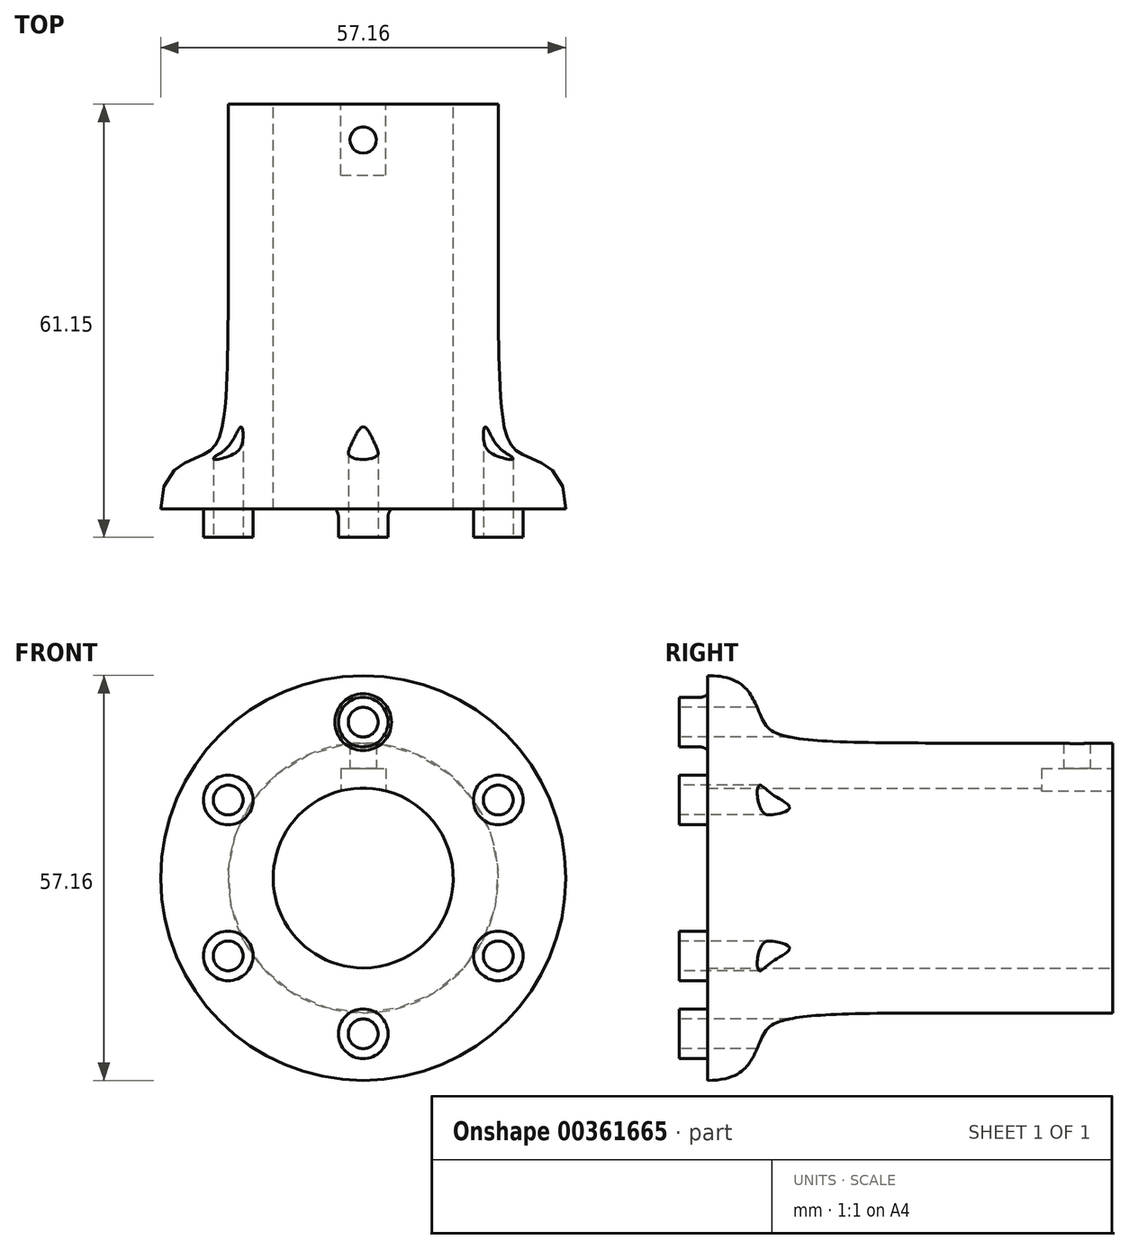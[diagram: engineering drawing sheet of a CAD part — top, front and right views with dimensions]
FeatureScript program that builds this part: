
annotation { "Feature Type Name" : "Feature", "Feature Type Description" : "" }
export const myFeature = defineFeature(function(context is Context, id is Id, definition is map)
    precondition{}
    {
        {
            var Q0;
            Q0=qCreatedBy(makeId("Front.planeOp"),FACE);
            var sketch = newSketch(context, id + "F0", { "sketchPlane" : qUnion([Q0])});
            skCircle(sketch, "E0", {"center": v(0, 0) * mm, "radius": 12.7 * mm});
            skCircle(sketch, "E1", {"center": v(0, 0) * mm, "radius": 19.05 * mm});
            skSolve(sketch);
        }
        {
            var Q0;
            Q0=qSketchRegion(id+"F0",true);
            extrude(context, id + "F1", {"entities" : qUnion([Q0]), "depth" : 25.4 * mm});
        }
        {
            var Q0;
            Q0=qCreatedBy(makeId("Front.planeOp"),FACE);
            cPlane(context, id + "F2", {"entities" : qUnion([Q0]), "cplaneType" : CPlaneType.OFFSET, "offset" : 50.8 * mm, "width" : 152.4 * mm, "height" : 152.4 * mm});
        }
        {
            var Q0;
            Q0=qCreatedBy(id+"F2.planeOp",FACE);
            var sketch = newSketch(context, id + "F3", { "sketchPlane" : qUnion([Q0])});
            skCircle(sketch, "E2", {"center": v(0, 0) * mm, "radius": 25.4 * mm});
            skCircle(sketch, "E3", {"center": v(0, 0) * mm, "radius": 6.35 * mm});
            skSolve(sketch);
        }
        {
            var Q0;
            Q0=qCreatedBy(makeId("Top.planeOp"),FACE);
            var sketch = newSketch(context, id + "F4", { "sketchPlane" : qUnion([Q0])});
            skLineSegment(sketch, "E4", {"start": v(0, 54.57) * mm, "end": v(0, 8.8) * mm, "construction": true});
            skSolve(sketch);
        }
        {
            var Q0;
            Q0=makeQuery(id+"F1.opExtrude","CAP_FACE",FACE,{"disambiguationData":[OSD([sQuery(id+"F0.wireOp",EDGE,"E0"),sQuery(id+"F0.wireOp",EDGE,"E1")])],"isStart":true});
            var sketch = newSketch(context, id + "F5", { "sketchPlane" : qUnion([Q0])});
            skLineSegment(sketch, "E5.bottom", {"start": v(3.18, 15.47) * mm, "end": v(-3.17, 15.47) * mm});
            skLineSegment(sketch, "E5.top", {"start": v(3.18, 9.12) * mm, "end": v(-3.17, 9.12) * mm});
            skLineSegment(sketch, "E5.left", {"start": v(3.18, 15.47) * mm, "end": v(3.18, 9.12) * mm});
            skLineSegment(sketch, "E5.right", {"start": v(-3.17, 15.47) * mm, "end": v(-3.17, 9.12) * mm});
            skPoint(sketch, "E5.middle", {"position": v(0, 12.3) * mm});
            skPoint(sketch, "E6", {"position": v(3.18, 12.3) * mm});
            skPoint(sketch, "E7", {"position": v(-3.17, 12.3) * mm});
            skSolve(sketch);
        }
        {
            var Q0;
            Q0=qSketchRegion(id+"F5",true);
            extrude(context, id + "F6", {"entities" : qUnion([Q0]), "operationType" : NewBodyOperationType.REMOVE, "oppositeDirection" : true, "depth" : 10 * mm, "offsetDistance" : 25.4 * mm});
        }
        {
            var Q0;
            Q0=qCreatedBy(makeId("Top.planeOp"),FACE);
            var sketch = newSketch(context, id + "F7", { "sketchPlane" : qUnion([Q0])});
            skCircle(sketch, "E8", {"center": v(0, -5.04) * mm, "radius": 1.87 * mm});
            skSolve(sketch);
        }
        {
            var Q0;
            Q0=makeQuery(id+"F1.opExtrude","CAP_FACE",FACE,{"disambiguationData":[OSD([sQuery(id+"F0.wireOp",EDGE,"E0"),sQuery(id+"F0.wireOp",EDGE,"E1")])],"isStart":false});
            var sketch = newSketch(context, id + "F8", { "sketchPlane" : qUnion([Q0])});
            skCircle(sketch, "E9.0", {"center": v(0, 0) * mm, "radius": 19.05 * mm});
            skSolve(sketch);
        }
        {
            var Q0;
            Q0=qSketchRegion(id+"F7",true);
            extrude(context, id + "F9", {"entities" : qUnion([Q0]), "operationType" : NewBodyOperationType.REMOVE, "depth" : 25.4 * mm, "offsetDistance" : 25.4 * mm});
        }
        {
            var Q0;
            Q0=qCreatedBy(id+"F2.planeOp",FACE);
            var sketch = newSketch(context, id + "F10", { "sketchPlane" : qUnion([Q0])});
            skCircle(sketch, "E10", {"center": v(0, 0) * mm, "radius": 25.4 * mm});
            skSolve(sketch);
        }
        {
            var Q0;
            Q0=qCreatedBy(id+"F2.planeOp",FACE);
            cPlane(context, id + "F11", {"entities" : qUnion([Q0]), "cplaneType" : CPlaneType.OFFSET, "offset" : 6.35 * mm, "width" : 152.4 * mm, "height" : 152.4 * mm});
        }
        {
            var Q0;
            Q0=qCreatedBy(id+"F11.planeOp",FACE);
            var sketch = newSketch(context, id + "F12", { "sketchPlane" : qUnion([Q0])});
            skCircle(sketch, "E11", {"center": v(0, 0) * mm, "radius": 28.58 * mm});
            skSolve(sketch);
        }
        {
            var Q1;
            Q1 = qSketchRegion(id + "F8", true);
            var Q2;
            Q2 = qSketchRegion(id + "F10", true);
            var Q3;
            Q3 = qSketchRegion(id + "F12", true);
            loft(context, id + "F13", {"operationType" : NewBodyOperationType.ADD, "startCondition" : LoftEndDerivativeType.NORMAL_TO_PROFILE, "startMagnitude" : 3, "endCondition" : LoftEndDerivativeType.NORMAL_TO_PROFILE, "endMagnitude" : 2, "sheetProfilesArray" : [{ "sheetProfileEntities" : qUnion([Q1]) }, { "sheetProfileEntities" : qUnion([Q2]) }, { "sheetProfileEntities" : qUnion([Q3]) }]});
        }
        {
            var Q0;
            Q0=makeQuery(id+"F1.opExtrude","CAP_FACE",FACE,{"disambiguationData":[OSD([sQuery(id+"F0.wireOp",EDGE,"E0"),sQuery(id+"F0.wireOp",EDGE,"E1")])],"isStart":true});
            var sketch = newSketch(context, id + "F14", { "sketchPlane" : qUnion([Q0])});
            skCircle(sketch, "E12", {"center": v(0, 0) * mm, "radius": 12.7 * mm});
            skSolve(sketch);
        }
        {
            var Q0;
            Q0 = qSketchRegion(id + "F14", true);
            extrude(context, id + "F15", {"entities" : qUnion([Q0]), "operationType" : NewBodyOperationType.REMOVE, "endBound" : BoundingType.THROUGH_ALL, "oppositeDirection" : true, "depth" : 25.4 * mm, "offsetDistance" : 25.4 * mm});
        }
        {
            var Q0;
            Q0=makeQuery(id+"F13.opLoft","CAP_FACE",FACE,{"disambiguationData":[OSD([makeQuery(id+"F12.imprint","IMPRINT",FACE,{"disambiguationData":[TD([[makeQuery(id+"F12.imprint","IMPRINT",EDGE,{"derivedFrom":sQuery(id+"F12.wireOp",EDGE,"E11")}),1.0]])]})])],"isStart":true});
            var sketch = newSketch(context, id + "F16", { "sketchPlane" : qUnion([Q0])});
            skCircle(sketch, "E13", {"center": v(0, 22) * mm, "radius": 3.5 * mm});
            skCircle(sketch, "E14.1.0", {"center": v(-19.05, 11) * mm, "radius": 3.5 * mm});
            skCircle(sketch, "E14.2.0", {"center": v(-19.05, -11) * mm, "radius": 3.5 * mm});
            skCircle(sketch, "E14.3.0", {"center": v(0, -22) * mm, "radius": 3.5 * mm});
            skCircle(sketch, "E14.4.0", {"center": v(19.05, -11) * mm, "radius": 3.5 * mm});
            skCircle(sketch, "E14.5.0", {"center": v(19.05, 11) * mm, "radius": 3.5 * mm});
            skPoint(sketch, "E14.center", {"position": v(0, 0) * mm});
            skSolve(sketch);
        }
        {
            var Q0;
            Q0 = qSketchRegion(id + "F16", true);
            extrude(context, id + "F17", {"entities" : qUnion([Q0]), "operationType" : NewBodyOperationType.ADD, "depth" : 4 * mm, "offsetDistance" : 25 * mm});
        }
        {
            var Q0;
            Q0=makeQuery(id+"F17.opExtrude","CAP_FACE",FACE,{"disambiguationData":[OSD([sQuery(id+"F16.wireOp",EDGE,"E13")])],"isStart":false});
            var sketch = newSketch(context, id + "F18", { "sketchPlane" : qUnion([Q0])});
            skCircle(sketch, "E15", {"center": v(0, 22) * mm, "radius": 2.1 * mm});
            skCircle(sketch, "E16.1.0", {"center": v(-19.05, 11) * mm, "radius": 2.1 * mm});
            skCircle(sketch, "E16.2.0", {"center": v(-19.05, -11) * mm, "radius": 2.1 * mm});
            skCircle(sketch, "E16.3.0", {"center": v(0, -22) * mm, "radius": 2.1 * mm});
            skCircle(sketch, "E16.4.0", {"center": v(19.05, -11) * mm, "radius": 2.1 * mm});
            skCircle(sketch, "E16.5.0", {"center": v(19.05, 11) * mm, "radius": 2.1 * mm});
            skPoint(sketch, "E16.center", {"position": v(0, 0) * mm});
            skSolve(sketch);
        }
        {
            var Q0;
            Q0=makeQuery(id+"F17.opExtrude","CAP_FACE",FACE,{"disambiguationData":[OSD([sQuery(id+"F16.wireOp",EDGE,"E13")])],"isStart":false});
            cPlane(context, id + "F19", {"entities" : qUnion([Q0]), "cplaneType" : CPlaneType.OFFSET, "offset" : 3 * mm, "oppositeDirection" : true, "width" : 150 * mm, "height" : 150 * mm});
        }
        {
            var Q0;
            Q0=qCreatedBy(id+"F19.planeOp",FACE);
            var sketch = newSketch(context, id + "F20", { "sketchPlane" : qUnion([Q0])});
            skCircle(sketch, "E17.0", {"center": v(0, 22) * mm, "radius": 3.5 * mm});
            skSolve(sketch);
        }
        {
            var Q0;
            Q0=makeQuery(id+"F13.opLoft","CAP_FACE",FACE,{"disambiguationData":[OSD([makeQuery(id+"F12.imprint","IMPRINT",FACE,{"disambiguationData":[TD([[makeQuery(id+"F12.imprint","IMPRINT",EDGE,{"derivedFrom":sQuery(id+"F12.wireOp",EDGE,"E11")}),1.0]])]})])],"isStart":true});
            var sketch = newSketch(context, id + "F21", { "sketchPlane" : qUnion([Q0])});
            skCircle(sketch, "E18", {"center": v(0, 22) * mm, "radius": 4 * mm});
            skSolve(sketch);
        }
        {
            var Q1;
            Q1 = qSketchRegion(id + "F20", true);
            var Q2;
            Q2 = qSketchRegion(id + "F21", true);
            loft(context, id + "F22", {"operationType" : NewBodyOperationType.ADD, "startCondition" : LoftEndDerivativeType.NORMAL_TO_PROFILE, "startMagnitude" : 1, "endCondition" : LoftEndDerivativeType.TANGENT_TO_PROFILE, "endMagnitude" : 1, "sheetProfilesArray" : [{ "sheetProfileEntities" : qUnion([Q1]) }, { "sheetProfileEntities" : qUnion([Q2]) }]});
        }
        {
            var Q0;
            Q0 = qSketchRegion(id + "F18", true);
            extrude(context, id + "F23", {"entities" : qUnion([Q0]), "operationType" : NewBodyOperationType.REMOVE, "endBound" : BoundingType.UP_TO_NEXT, "oppositeDirection" : true, "depth" : 25 * mm, "offsetDistance" : 25 * mm});
        }
    });
